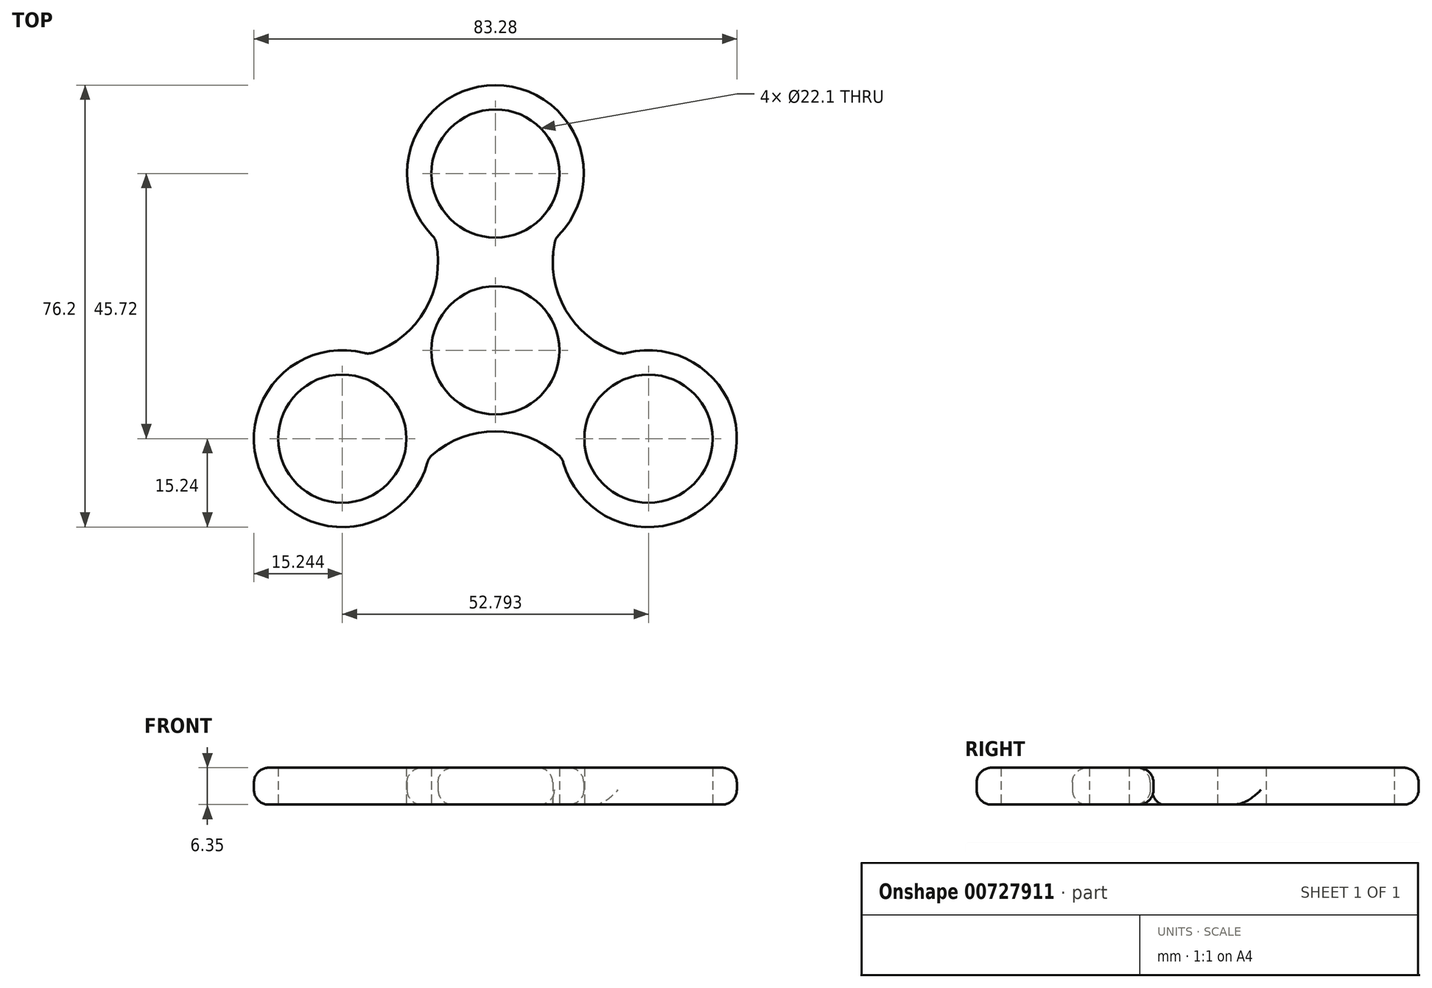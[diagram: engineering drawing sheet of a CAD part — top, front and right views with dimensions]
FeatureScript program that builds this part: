
annotation { "Feature Type Name" : "Feature", "Feature Type Description" : "" }
export const myFeature = defineFeature(function(context is Context, id is Id, definition is map)
    precondition{}
    {
        {
            var Q0;
            Q0=qCreatedBy(makeId("Top.planeOp"),FACE);
            var sketch = newSketch(context, id + "F0", { "sketchPlane" : qUnion([Q0])});
            skCircle(sketch, "E0", {"center": v(0, 0) * mm, "radius": 11.05 * mm});
            skCircle(sketch, "E1", {"center": v(0, 0) * mm, "radius": 13.97 * mm});
            skLineSegment(sketch, "E2", {"start": v(0, 0) * mm, "end": v(0, 30.48) * mm});
            skCircle(sketch, "E3", {"center": v(0, 30.48) * mm, "radius": 11.05 * mm});
            skCircle(sketch, "E4", {"center": v(0, 30.48) * mm, "radius": 15.24 * mm});
            skCircle(sketch, "E5.1.0", {"center": v(-26.4, -15.24) * mm, "radius": 11.05 * mm});
            skCircle(sketch, "E5.1.1", {"center": v(-26.4, -15.24) * mm, "radius": 15.24 * mm});
            skCircle(sketch, "E5.2.0", {"center": v(26.4, -15.24) * mm, "radius": 11.05 * mm});
            skCircle(sketch, "E5.2.1", {"center": v(26.4, -15.24) * mm, "radius": 15.24 * mm});
            skLineSegment(sketch, "E6", {"start": v(0, 0) * mm, "end": v(-26.4, 15.24) * mm});
            skArc(sketch, "E7", {"start": v(-30.84, -0.66) * mm, "mid": v(-12.1, 6.98) * mm, "end": v(-14.85, 27.04) * mm});
            skArc(sketch, "E8.1.0", {"start": v(16, -26.38) * mm, "mid": v(0, -13.97) * mm, "end": v(-16, -26.38) * mm});
            skArc(sketch, "E8.2.0", {"start": v(14.85, 27.04) * mm, "mid": v(12.1, 6.99) * mm, "end": v(30.84, -0.66) * mm});
            skSolve(sketch);
        }
        {
            var Q0;
            Q0 = qSketchRegion(id + "F0", true);
            extrude(context, id + "F1", {"entities" : qUnion([Q0]), "depth" : 6.35 * mm, "offsetDistance" : 25.4 * mm});
        }
        {
            var Q0;
            Q0=makeQuery(id+"F1.opExtrude","CAP_EDGE",EDGE,{"disambiguationData":[OSD([sQuery(id+"F0.wireOp",EDGE,"E7")])],"isStart":false});
            var Q1;
            Q1=makeQuery(id+"F1.opExtrude","CAP_EDGE",EDGE,{"disambiguationData":[OSD([sQuery(id+"F0.wireOp",EDGE,"E4")])],"isStart":false});
            var Q2;
            Q2=makeQuery(id+"F1.opExtrude","CAP_EDGE",EDGE,{"disambiguationData":[OSD([sQuery(id+"F0.wireOp",EDGE,"E8.2.0")])],"isStart":false});
            var Q3;
            Q3=makeQuery(id+"F1.opExtrude","CAP_EDGE",EDGE,{"disambiguationData":[OSD([sQuery(id+"F0.wireOp",EDGE,"E5.2.1")])],"isStart":false});
            var Q4;
            Q4=makeQuery(id+"F1.opExtrude","CAP_EDGE",EDGE,{"disambiguationData":[OSD([sQuery(id+"F0.wireOp",EDGE,"E8.1.0")])],"isStart":false});
            var Q5;
            Q5=makeQuery(id+"F1.opExtrude","CAP_EDGE",EDGE,{"disambiguationData":[OSD([sQuery(id+"F0.wireOp",EDGE,"E5.1.1")])],"isStart":false});
            var Q6;
            Q6=makeQuery(id+"F1.opExtrude","CAP_EDGE",EDGE,{"disambiguationData":[OSD([sQuery(id+"F0.wireOp",EDGE,"E5.1.1")])],"isStart":true});
            var Q7;
            Q7=makeQuery(id+"F1.opExtrude","SWEPT_FACE",FACE,{"disambiguationData":[OSD([sQuery(id+"F0.wireOp",EDGE,"E5.1.1")])]});
            var Q8;
            Q8=makeQuery(id+"F1.opExtrude","SWEPT_FACE",FACE,{"disambiguationData":[OSD([sQuery(id+"F0.wireOp",EDGE,"E4")])]});
            var Q9;
            Q9=makeQuery(id+"F1.opExtrude","SWEPT_FACE",FACE,{"disambiguationData":[OSD([sQuery(id+"F0.wireOp",EDGE,"E8.1.0")])]});
            var Q10;
            Q10=makeQuery(id+"F1.opExtrude","SWEPT_FACE",FACE,{"disambiguationData":[OSD([sQuery(id+"F0.wireOp",EDGE,"E5.2.1")])]});
            var Q11;
            Q11=makeQuery(id+"F1.opExtrude","CAP_EDGE",EDGE,{"disambiguationData":[OSD([sQuery(id+"F0.wireOp",EDGE,"E7")])],"isStart":true});
            fillet(context, id + "F2", {"entities" : qUnion([Q0, Q1, Q2, Q3, Q4, Q5, Q6, Q7, Q8, Q9, Q10, Q11]), "radius" : 2.54 * mm, "tangentPropagation" : true, "allowEdgeOverflow" : false});
        }
    });
